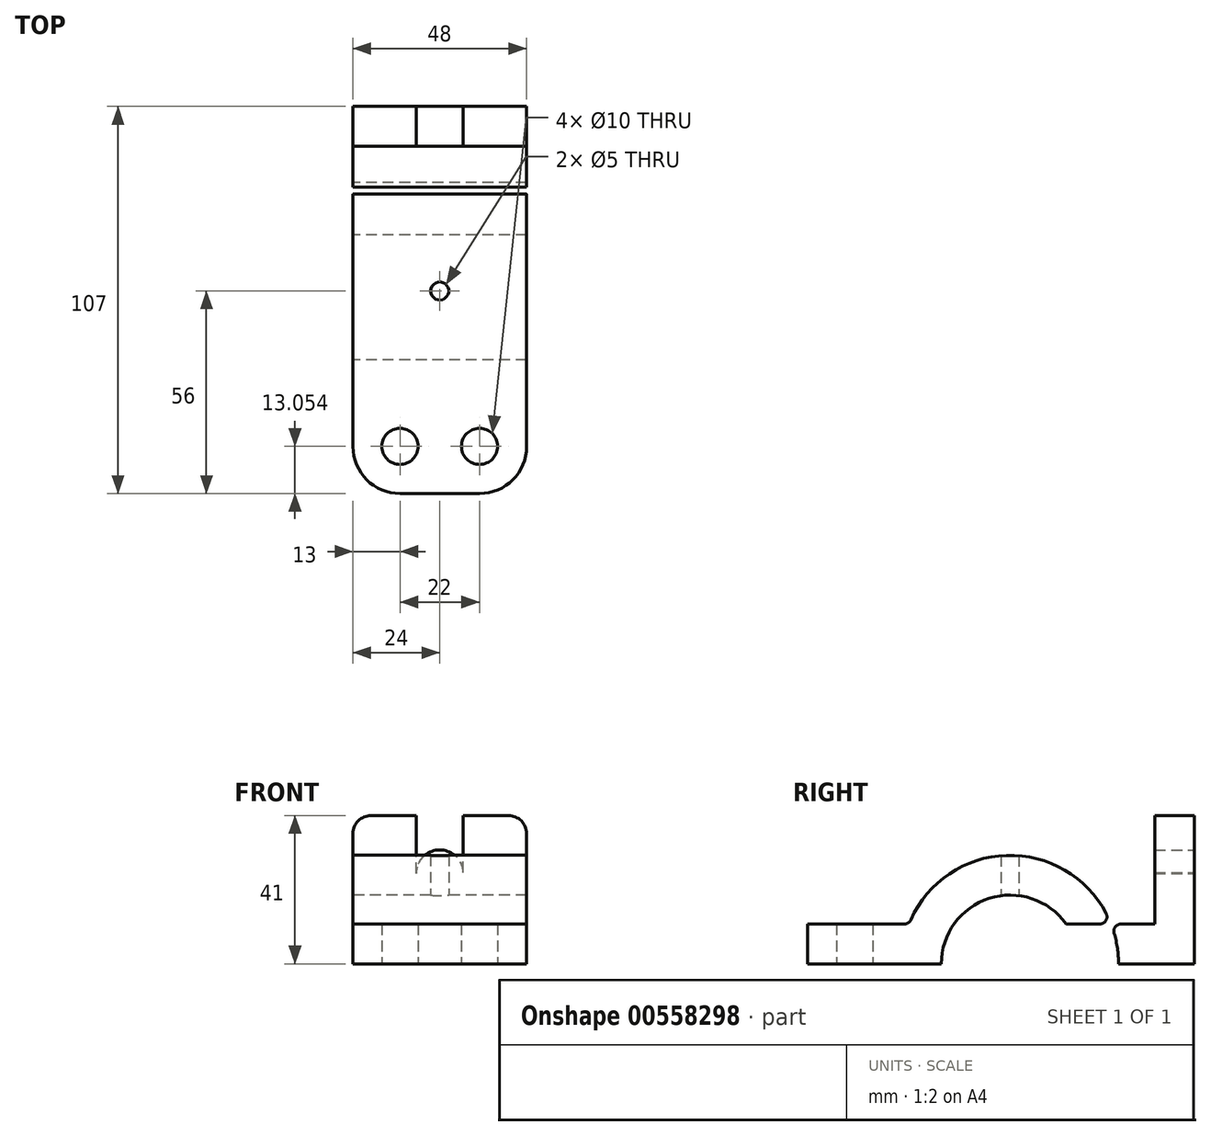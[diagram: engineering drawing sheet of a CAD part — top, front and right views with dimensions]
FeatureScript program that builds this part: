
annotation { "Feature Type Name" : "Feature", "Feature Type Description" : "" }
export const myFeature = defineFeature(function(context is Context, id is Id, definition is map)
    precondition{}
    {
        {
            var Q0;
            Q0=qCreatedBy(makeId("Right.planeOp"),FACE);
            var sketch = newSketch(context, id + "F0", { "sketchPlane" : qUnion([Q0])});
            skCircle(sketch, "E0", {"center": v(0, 0) * mm, "radius": 19 * mm});
            skCircle(sketch, "E1", {"center": v(0, 0) * mm, "radius": 30 * mm});
            skLineSegment(sketch, "E2.bottom", {"start": v(-56, 0) * mm, "end": v(51, 0) * mm});
            skLineSegment(sketch, "E2.top", {"start": v(-56, 11) * mm, "end": v(51, 11) * mm});
            skLineSegment(sketch, "E2.left", {"start": v(-56, 0) * mm, "end": v(-56, 11) * mm});
            skLineSegment(sketch, "E2.right", {"start": v(51, 0) * mm, "end": v(51, 11) * mm});
            skLineSegment(sketch, "E3.bottom", {"start": v(27.91, 11) * mm, "end": v(51, 11) * mm});
            skLineSegment(sketch, "E3.top", {"start": v(40, 41) * mm, "end": v(51, 41) * mm});
            skLineSegment(sketch, "E3.left", {"start": v(40, 11) * mm, "end": v(40, 41) * mm});
            skLineSegment(sketch, "E3.right", {"start": v(51, 11) * mm, "end": v(51, 41) * mm});
            skSolve(sketch);
        }
        {
            var Q0;
            {var subQ5=sQuery(id+"F0.wireOp",EDGE,"E2.left");Q0=makeQuery(id+"F0.imprint","IMPRINT",FACE,{"disambiguationData":[TD([[makeQuery(id+"F0.imprint","IMPRINT",EDGE,{"derivedFrom":subQ5}),-1.0]])]});}
            var Q1;
            {var subQ0=sQuery(id+"F0.wireOp",EDGE,"E2.top");var subQ1=sQuery(id+"F0.wireOp",EDGE,"E0");var subQ2=makeQuery(id+"F0.imprint","INTERSECT",VERTEX,{"disambiguationData":[OD(1.0)],"derivedFrom":[subQ1,subQ0]});Q1=makeQuery(id+"F0.imprint","IMPRINT",FACE,{"disambiguationData":[TD([[makeQuery(id+"F0.imprint","IMPRINT",EDGE,{"disambiguationData":[TD([[subQ2,-1.0]])],"derivedFrom":subQ1}),-1.0]])]});}
            var Q2;
            {var subQ0=sQuery(id+"F0.wireOp",EDGE,"E2.top");var subQ1=sQuery(id+"F0.wireOp",EDGE,"E0");var subQ2=makeQuery(id+"F0.imprint","INTERSECT",VERTEX,{"disambiguationData":[OD(0.0)],"derivedFrom":[subQ1,subQ0]});Q2=makeQuery(id+"F0.imprint","IMPRINT",FACE,{"disambiguationData":[TD([[makeQuery(id+"F0.imprint","IMPRINT",EDGE,{"disambiguationData":[TD([[subQ2,-1.0]])],"derivedFrom":subQ1}),-1.0]])]});}
            var Q3;
            {var subQ0=sQuery(id+"F0.wireOp",EDGE,"E2.top");var subQ1=sQuery(id+"F0.wireOp",EDGE,"E0");var subQ2=makeQuery(id+"F0.imprint","INTERSECT",VERTEX,{"disambiguationData":[OD(0.0)],"derivedFrom":[subQ1,subQ0]});Q3=makeQuery(id+"F0.imprint","IMPRINT",FACE,{"disambiguationData":[TD([[makeQuery(id+"F0.imprint","IMPRINT",EDGE,{"disambiguationData":[TD([[subQ2,1.0]])],"derivedFrom":subQ1}),-1.0]])]});}
            var Q4;
            {var subQ0=sQuery(id+"F0.wireOp",EDGE,"E2.right");Q4=makeQuery(id+"F0.imprint","IMPRINT",FACE,{"disambiguationData":[TD([[makeQuery(id+"F0.imprint","IMPRINT",EDGE,{"derivedFrom":subQ0}),1.0]])]});}
            var Q5;
            Q5=makeQuery(id+"F0.imprint","IMPRINT",FACE,{"disambiguationData":[TD([[makeQuery(id+"F0.imprint","IMPRINT",EDGE,{"derivedFrom":sQuery(id+"F0.wireOp",EDGE,"E3.top")}),-1.0]])]});
            extrude(context, id + "F1", {"entities" : qUnion([Q0, Q1, Q2, Q3, Q4, Q5]), "endBound" : BoundingType.SYMMETRIC, "depth" : 48 * mm, "offsetDistance" : 25 * mm});
        }
        {
            var Q0;
            Q0=makeQuery(id+"F1.opExtrude","SWEPT_FACE",FACE,{"disambiguationData":[OSD([sQuery(id+"F0.wireOp",EDGE,"E2.right"),sQuery(id+"F0.wireOp",EDGE,"E3.right")])]});
            var sketch = newSketch(context, id + "F2", { "sketchPlane" : qUnion([Q0])});
            skLineSegment(sketch, "E4", {"start": v(0, 0) * mm, "end": v(0, 41) * mm, "construction": true});
            skCircle(sketch, "E5", {"center": v(0, 25) * mm, "radius": 6.5 * mm});
            skLineSegment(sketch, "E6", {"start": v(-6.5, 24.73) * mm, "end": v(-6.5, 41) * mm});
            skLineSegment(sketch, "E7", {"start": v(6.5, 25) * mm, "end": v(6.5, 41) * mm});
            skSolve(sketch);
        }
        {
            var Q0;
            {var subQ0=sQuery(id+"F2.wireOp",EDGE,"E5");var subQ5=makeQuery(id+"F2.imprint","IMPRINT",VERTEX,{"derivedFrom":subQ0});Q0=makeQuery(id+"F2.imprint","IMPRINT",FACE,{"disambiguationData":[TD([[makeQuery(id+"F2.imprint","IMPRINT",EDGE,{"disambiguationData":[TD([[subQ5,1.0]])],"derivedFrom":subQ0}),1.0]])]});}
            var Q1;
            {var subQ0=sQuery(id+"F2.wireOp",EDGE,"E7");Q1=makeQuery(id+"F2.imprint","IMPRINT",FACE,{"disambiguationData":[TD([[makeQuery(id+"F2.imprint","IMPRINT",EDGE,{"derivedFrom":subQ0}),1.0]])]});}
            var Q2;
            Q2=makeQuery(id+"F1.opExtrude","SWEPT_BODY",BODY,{"disambiguationData":[OSD([sQuery(id+"F0.wireOp",EDGE,"E0"),sQuery(id+"F0.wireOp",EDGE,"E1"),sQuery(id+"F0.wireOp",EDGE,"E2.bottom"),sQuery(id+"F0.wireOp",EDGE,"E2.top"),sQuery(id+"F0.wireOp",EDGE,"E2.left"),sQuery(id+"F0.wireOp",EDGE,"E2.right"),sQuery(id+"F0.wireOp",EDGE,"E3.bottom"),sQuery(id+"F0.wireOp",EDGE,"E3.top"),sQuery(id+"F0.wireOp",EDGE,"E3.left"),sQuery(id+"F0.wireOp",EDGE,"E3.right")])]});
            extrude(context, id + "F3", {"entities" : qUnion([Q0, Q1]), "operationType" : NewBodyOperationType.REMOVE, "endBound" : BoundingType.UP_TO_BODY, "oppositeDirection" : true, "depth" : 25 * mm, "endBoundEntityBody" : qUnion([Q2]), "offsetDistance" : 25 * mm});
        }
        {
            var Q0;
            Q0=qCreatedBy(makeId("Top.planeOp"),FACE);
            var sketch = newSketch(context, id + "F4", { "sketchPlane" : qUnion([Q0])});
            skCircle(sketch, "E8", {"center": v(0, 0) * mm, "radius": 2.5 * mm});
            skLineSegment(sketch, "E9", {"start": v(0, -55.82) * mm, "end": v(0, -27.93) * mm, "construction": true});
            skLineSegment(sketch, "E10", {"start": v(-22.4, -42.95) * mm, "end": v(25.79, -42.95) * mm, "construction": true});
            skCircle(sketch, "E11", {"center": v(-11, -42.95) * mm, "radius": 5 * mm});
            skCircle(sketch, "E12", {"center": v(11, -42.95) * mm, "radius": 5 * mm});
            skSolve(sketch);
        }
        {
            var Q0;
            Q0=makeQuery(id+"F4.imprint","IMPRINT",FACE,{"disambiguationData":[TD([[makeQuery(id+"F4.imprint","IMPRINT",EDGE,{"derivedFrom":sQuery(id+"F4.wireOp",EDGE,"E12")}),1.0]])]});
            var Q1;
            Q1=makeQuery(id+"F4.imprint","IMPRINT",FACE,{"disambiguationData":[TD([[makeQuery(id+"F4.imprint","IMPRINT",EDGE,{"derivedFrom":sQuery(id+"F4.wireOp",EDGE,"E11")}),1.0]])]});
            var Q2;
            Q2=makeQuery(id+"F4.imprint","IMPRINT",FACE,{"disambiguationData":[TD([[makeQuery(id+"F4.imprint","IMPRINT",EDGE,{"derivedFrom":sQuery(id+"F4.wireOp",EDGE,"E8")}),1.0]])]});
            extrude(context, id + "F5", {"entities" : qUnion([Q0, Q1, Q2]), "operationType" : NewBodyOperationType.REMOVE, "endBound" : BoundingType.THROUGH_ALL, "depth" : 25 * mm, "offsetDistance" : 25 * mm});
        }
        {
            var Q0;
            Q0=makeQuery(id+"F1.opExtrude","CAP_EDGE",EDGE,{"disambiguationData":[OSD([sQuery(id+"F0.wireOp",EDGE,"E2.left")])],"isStart":true});
            var Q1;
            Q1=makeQuery(id+"F1.opExtrude","CAP_EDGE",EDGE,{"disambiguationData":[OSD([sQuery(id+"F0.wireOp",EDGE,"E2.left")])],"isStart":false});
            fillet(context, id + "F6", {"entities" : qUnion([Q0, Q1]), "radius" : 13 * mm, "tangentPropagation" : true, "allowEdgeOverflow" : false});
        }
        {
            var Q0;
            Q0=makeQuery(id+"F1.opExtrude","CAP_EDGE",EDGE,{"disambiguationData":[OSD([sQuery(id+"F0.wireOp",EDGE,"E3.top")])],"isStart":true});
            var Q1;
            Q1=makeQuery(id+"F1.opExtrude","CAP_EDGE",EDGE,{"disambiguationData":[OSD([sQuery(id+"F0.wireOp",EDGE,"E3.top")])],"isStart":false});
            fillet(context, id + "F7", {"entities" : qUnion([Q0, Q1]), "radius" : 5 * mm, "tangentPropagation" : true, "allowEdgeOverflow" : false});
        }
        {
            var Q0;
            Q0=makeQuery(id+"F1.opExtrude","SWEPT_EDGE",EDGE,{"disambiguationData":[OSD([sQuery(id+"F0.wireOp",EDGE,"E1"),sQuery(id+"F0.wireOp",EDGE,"E2.top")])]});
            var Q1;
            Q1=makeQuery(id+"F1.opExtrude","SWEPT_EDGE",EDGE,{"disambiguationData":[OSD([sQuery(id+"F0.wireOp",EDGE,"E1"),sQuery(id+"F0.wireOp",EDGE,"E2.top"),sQuery(id+"F0.wireOp",EDGE,"E3.bottom")])]});
            fillet(context, id + "F8", {"entities" : qUnion([Q0, Q1]), "radius" : 2 * mm, "tangentPropagation" : true, "allowEdgeOverflow" : false});
        }
    });
